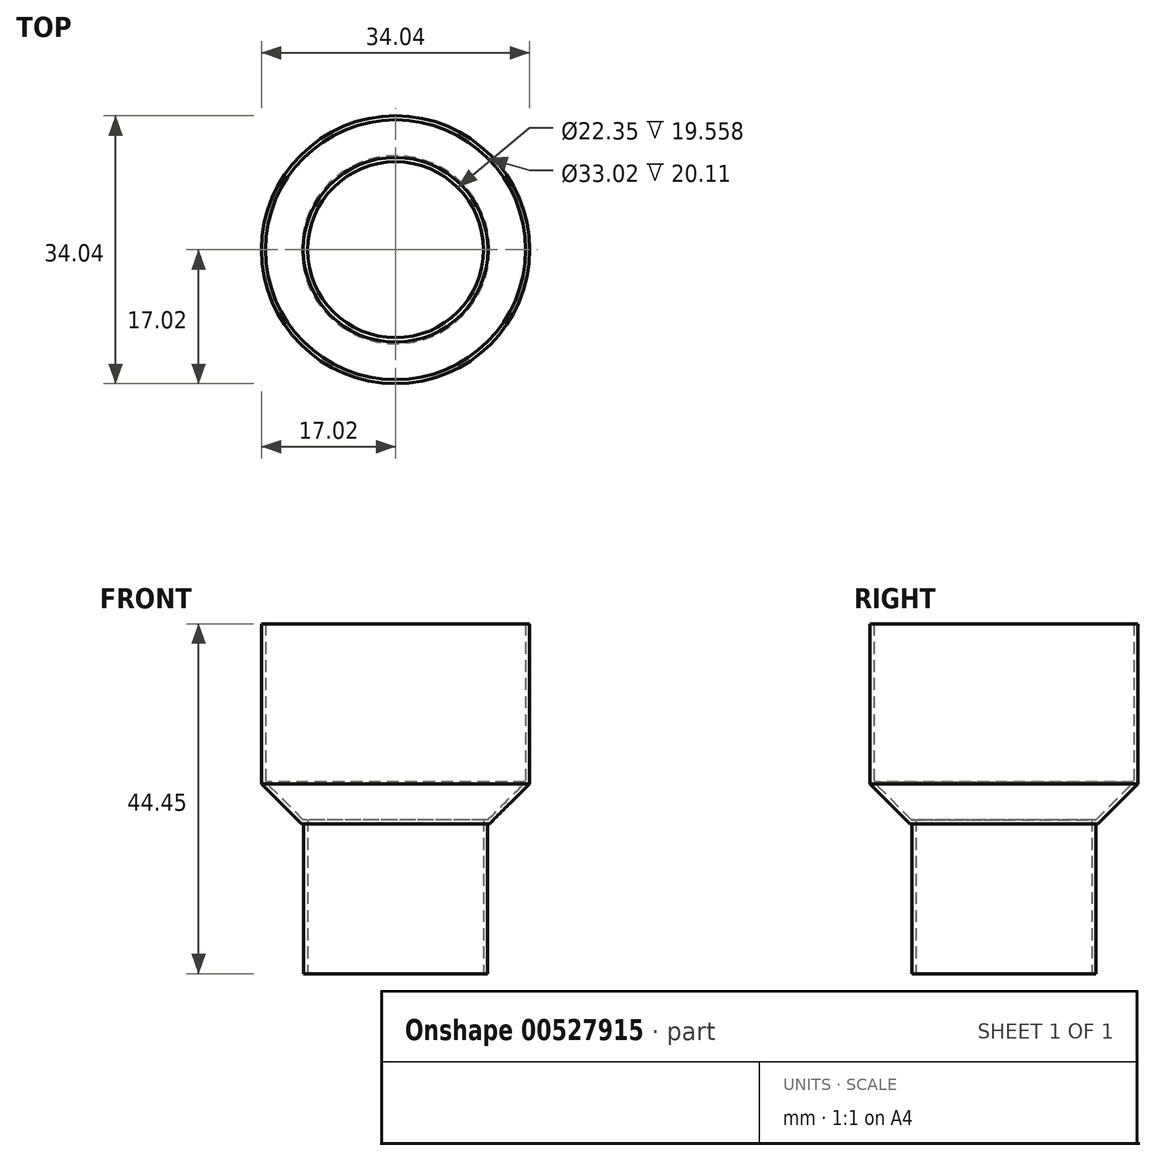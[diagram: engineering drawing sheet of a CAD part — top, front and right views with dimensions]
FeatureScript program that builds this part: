
annotation { "Feature Type Name" : "Feature", "Feature Type Description" : "" }
export const myFeature = defineFeature(function(context is Context, id is Id, definition is map)
    precondition{}
    {
        {
            var Q0;
            Q0=qCreatedBy(makeId("Top.planeOp"),FACE);
            var sketch = newSketch(context, id + "F0", { "sketchPlane" : qUnion([Q0])});
            skCircle(sketch, "E0", {"center": v(0, 0) * mm, "radius": 11.68 * mm});
            skSolve(sketch);
        }
        {
            var Q0;
            Q0=makeQuery(id+"F0.imprint","IMPRINT",FACE,{"disambiguationData":[TD([[makeQuery(id+"F0.imprint","IMPRINT",EDGE,{"derivedFrom":sQuery(id+"F0.wireOp",EDGE,"E0")}),1.0]])]});
            extrude(context, id + "F1", {"entities" : qUnion([Q0]), "depth" : 19.05 * mm, "offsetDistance" : 25.4 * mm});
        }
        {
            var Q0;
            Q0=makeQuery(id+"F1.opExtrude","CAP_FACE",FACE,{"disambiguationData":[OSD([sQuery(id+"F0.wireOp",EDGE,"E0")])],"isStart":false});
            var sketch = newSketch(context, id + "F2", { "sketchPlane" : qUnion([Q0])});
            skCircle(sketch, "E1", {"center": v(0, 0) * mm, "radius": 17.02 * mm});
            skSolve(sketch);
        }
        {
            var Q0;
            Q0=makeQuery(id+"F2.imprint","IMPRINT",FACE,{"disambiguationData":[TD([[makeQuery(id+"F2.imprint","IMPRINT",EDGE,{"derivedFrom":makeQuery(id+"F1.opExtrude","CAP_EDGE",EDGE,{"disambiguationData":[OSD([sQuery(id+"F0.wireOp",EDGE,"E0")])],"isStart":false})}),1.0]])]});
            var Q1;
            Q1=makeQuery(id+"F2.imprint","IMPRINT",FACE,{"disambiguationData":[TD([[makeQuery(id+"F2.imprint","IMPRINT",EDGE,{"derivedFrom":sQuery(id+"F2.wireOp",EDGE,"E1")}),1.0]])]});
            extrude(context, id + "F3", {"entities" : qUnion([Q0, Q1]), "operationType" : NewBodyOperationType.ADD, "depth" : 25.4 * mm, "offsetDistance" : 25.4 * mm});
        }
        {
            var Q0;
            Q0=makeQuery(id+"F3.opExtrude","CAP_EDGE",EDGE,{"disambiguationData":[OSD([sQuery(id+"F2.wireOp",EDGE,"E1")])],"isStart":true});
            chamfer(context, id + "F4", {"entities" : qUnion([Q0]), "chamferType" : ChamferType.TWO_OFFSETS, "width1" : 5.08 * mm, "oppositeDirection" : false, "width2" : 5.08 * mm, "tangentPropagation" : true});
        }
        {
            var Q0;
            Q0=makeQuery(id+"F3.opExtrude","CAP_FACE",FACE,{"disambiguationData":[OSD([sQuery(id+"F2.wireOp",EDGE,"E1")])],"isStart":false});
            var Q1;
            Q1=makeQuery(id+"F1.opExtrude","CAP_FACE",FACE,{"disambiguationData":[OSD([sQuery(id+"F0.wireOp",EDGE,"E0")])],"isStart":true});
            shell(context, id + "F5", {"entities" : qUnion([Q0, Q1]), "thickness" : 0.5 * mm});
        }
    });
